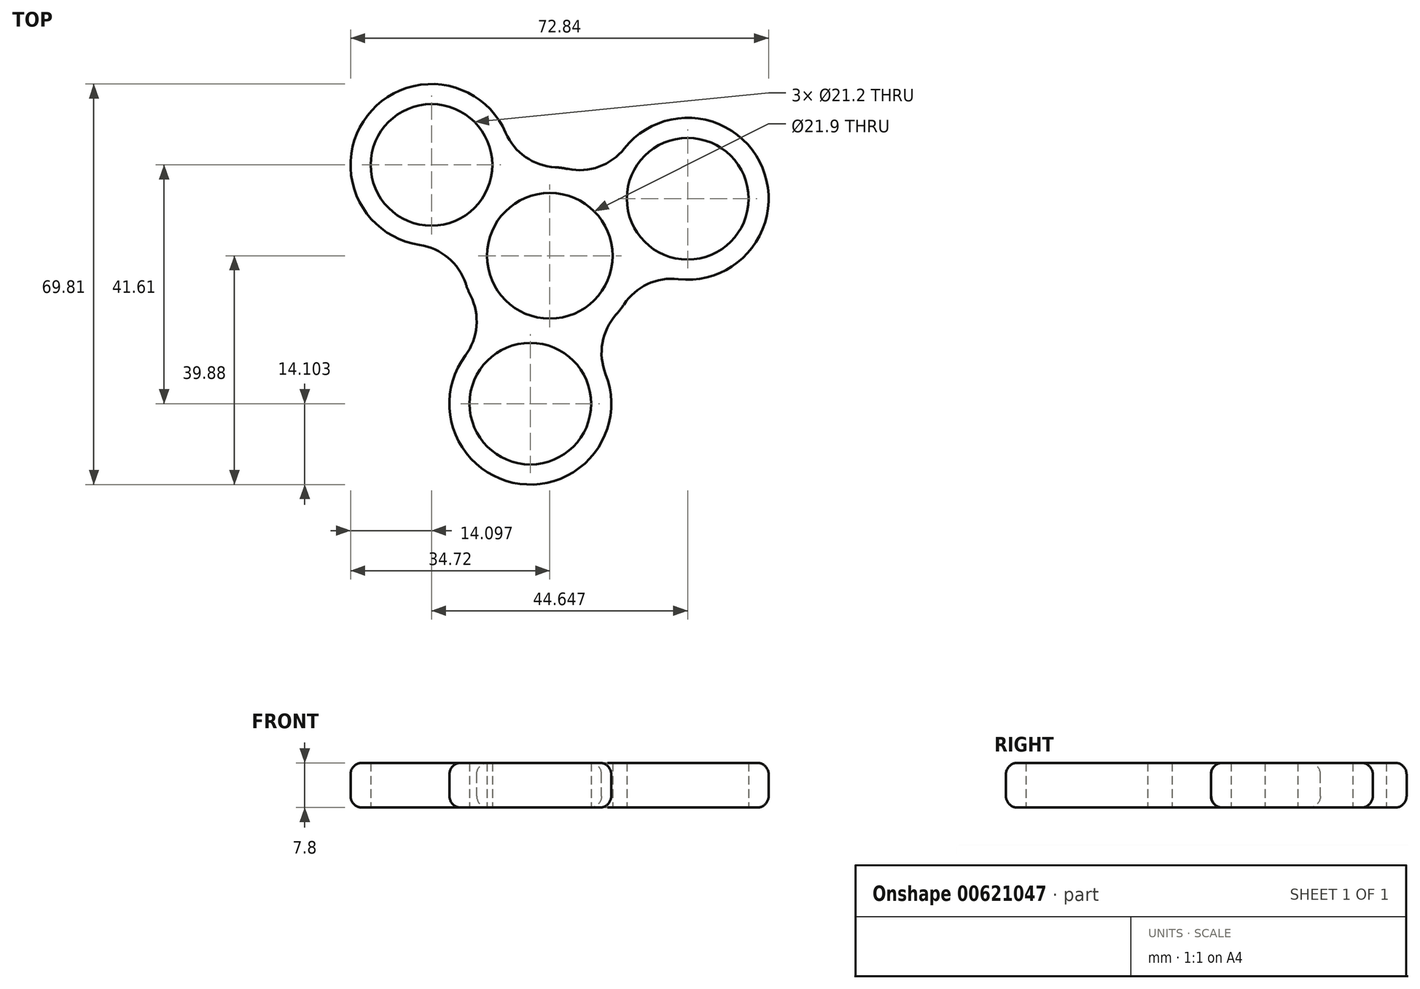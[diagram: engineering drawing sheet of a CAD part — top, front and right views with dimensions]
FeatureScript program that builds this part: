
annotation { "Feature Type Name" : "Feature", "Feature Type Description" : "" }
export const myFeature = defineFeature(function(context is Context, id is Id, definition is map)
    precondition{}
    {
        {
            var Q0;
            Q0=qCreatedBy(makeId("Top.planeOp"),FACE);
            var sketch = newSketch(context, id + "F0", { "sketchPlane" : qUnion([Q0])});
            skCircle(sketch, "E0", {"center": v(0, 0) * mm, "radius": 10.95 * mm});
            skCircle(sketch, "E1.0", {"center": v(0, 0) * mm, "radius": 15.45 * mm});
            skCircle(sketch, "E2.cCircle", {"center": v(0, 0) * mm, "radius": 13 * mm, "construction": true});
            skLineSegment(sketch, "E2.0", {"start": v(-20.62, 15.83) * mm, "end": v(24.02, 9.94) * mm, "construction": true});
            skLineSegment(sketch, "E2.1", {"start": v(24.02, 9.94) * mm, "end": v(-3.4, -25.78) * mm, "construction": true});
            skLineSegment(sketch, "E2.2", {"start": v(-3.4, -25.78) * mm, "end": v(-20.62, 15.83) * mm, "construction": true});
            skPoint(sketch, "E2.0.midPoint", {"position": v(1.7, 12.89) * mm});
            skCircle(sketch, "E3", {"center": v(-20.62, 15.83) * mm, "radius": 10.6 * mm});
            skCircle(sketch, "E4", {"center": v(24.02, 9.94) * mm, "radius": 10.6 * mm});
            skCircle(sketch, "E5", {"center": v(-3.4, -25.78) * mm, "radius": 10.6 * mm});
            skCircle(sketch, "E6.0", {"center": v(-20.62, 15.83) * mm, "radius": 14.1 * mm});
            skCircle(sketch, "E7.0", {"center": v(24.02, 9.94) * mm, "radius": 14.1 * mm});
            skCircle(sketch, "E8.0", {"center": v(-3.4, -25.78) * mm, "radius": 14.1 * mm});
            skSolve(sketch);
        }
        {
            var Q0;
            Q0=qSketchRegion(id+"F0",true);
            extrude(context, id + "F1", {"entities" : qUnion([Q0]), "depth" : 7.8 * mm, "offsetDistance" : 25 * mm});
        }
        {
            var Q0;
            {var subQ0=sQuery(id+"F0.wireOp",EDGE,"E6.0");var subQ1=sQuery(id+"F0.wireOp",EDGE,"E1.0");Q0=makeQuery(id+"F1.opExtrude","SWEPT_EDGE",EDGE,{"disambiguationData":[OSD([subQ1,subQ0]),TDD([makeQuery(id+"F0.imprint","INTERSECT",VERTEX,{"disambiguationData":[OD(1.0)],"derivedFrom":[subQ1,subQ0]})])]});}
            var Q1;
            {var subQ0=sQuery(id+"F0.wireOp",EDGE,"E6.0");var subQ1=sQuery(id+"F0.wireOp",EDGE,"E1.0");Q1=makeQuery(id+"F1.opExtrude","SWEPT_EDGE",EDGE,{"disambiguationData":[OSD([subQ1,subQ0]),TDD([makeQuery(id+"F0.imprint","INTERSECT",VERTEX,{"disambiguationData":[OD(0.0)],"derivedFrom":[subQ1,subQ0]})])]});}
            var Q2;
            {var subQ0=sQuery(id+"F0.wireOp",EDGE,"E7.0");var subQ1=sQuery(id+"F0.wireOp",EDGE,"E1.0");Q2=makeQuery(id+"F1.opExtrude","SWEPT_EDGE",EDGE,{"disambiguationData":[OSD([subQ1,subQ0]),TDD([makeQuery(id+"F0.imprint","INTERSECT",VERTEX,{"disambiguationData":[OD(0.0)],"derivedFrom":[subQ1,subQ0]})])]});}
            var Q3;
            {var subQ0=sQuery(id+"F0.wireOp",EDGE,"E7.0");var subQ1=sQuery(id+"F0.wireOp",EDGE,"E1.0");Q3=makeQuery(id+"F1.opExtrude","SWEPT_EDGE",EDGE,{"disambiguationData":[OSD([subQ1,subQ0]),TDD([makeQuery(id+"F0.imprint","INTERSECT",VERTEX,{"disambiguationData":[OD(1.0)],"derivedFrom":[subQ1,subQ0]})])]});}
            var Q4;
            {var subQ0=sQuery(id+"F0.wireOp",EDGE,"E8.0");var subQ1=sQuery(id+"F0.wireOp",EDGE,"E1.0");Q4=makeQuery(id+"F1.opExtrude","SWEPT_EDGE",EDGE,{"disambiguationData":[OSD([subQ1,subQ0]),TDD([makeQuery(id+"F0.imprint","INTERSECT",VERTEX,{"disambiguationData":[OD(1.0)],"derivedFrom":[subQ1,subQ0]})])]});}
            var Q5;
            {var subQ0=sQuery(id+"F0.wireOp",EDGE,"E8.0");var subQ1=sQuery(id+"F0.wireOp",EDGE,"E1.0");Q5=makeQuery(id+"F1.opExtrude","SWEPT_EDGE",EDGE,{"disambiguationData":[OSD([subQ1,subQ0]),TDD([makeQuery(id+"F0.imprint","INTERSECT",VERTEX,{"disambiguationData":[OD(0.0)],"derivedFrom":[subQ1,subQ0]})])]});}
            fillet(context, id + "F2", {"entities" : qUnion([Q0, Q1, Q2, Q3, Q4, Q5]), "radius" : 10 * mm, "tangentPropagation" : true, "allowEdgeOverflow" : false});
        }
        {
            var Q0;
            {var subQ0=sQuery(id+"F0.wireOp",EDGE,"E7.0");var subQ1=sQuery(id+"F0.wireOp",EDGE,"E1.0");Q0=makeQuery(id+"F2.opFillet","BLEND_EDGE",EDGE,{"blendedFrom":[makeQuery(id+"F1.opExtrude","SWEPT_EDGE",EDGE,{"disambiguationData":[OSD([subQ1,subQ0]),TDD([makeQuery(id+"F0.imprint","INTERSECT",VERTEX,{"disambiguationData":[OD(1.0)],"derivedFrom":[subQ1,subQ0]})])]}),makeQuery(id+"F1.opExtrude","CAP_FACE",FACE,{"disambiguationData":[OSD([sQuery(id+"F0.wireOp",EDGE,"E0"),subQ1,sQuery(id+"F0.wireOp",EDGE,"E3"),sQuery(id+"F0.wireOp",EDGE,"E4"),sQuery(id+"F0.wireOp",EDGE,"E5"),sQuery(id+"F0.wireOp",EDGE,"E6.0"),subQ0,sQuery(id+"F0.wireOp",EDGE,"E8.0")])],"isStart":true})],"blendedInto":[makeQuery(id+"F1.opExtrude","CAP_FACE",FACE,{"disambiguationData":[OSD([sQuery(id+"F0.wireOp",EDGE,"E0"),subQ1,sQuery(id+"F0.wireOp",EDGE,"E3"),sQuery(id+"F0.wireOp",EDGE,"E4"),sQuery(id+"F0.wireOp",EDGE,"E5"),sQuery(id+"F0.wireOp",EDGE,"E6.0"),subQ0,sQuery(id+"F0.wireOp",EDGE,"E8.0")])],"isStart":true})]});}
            var Q1;
            {var subQ0=sQuery(id+"F0.wireOp",EDGE,"E8.0");var subQ1=sQuery(id+"F0.wireOp",EDGE,"E1.0");Q1=makeQuery(id+"F2.opFillet","BLEND_EDGE",EDGE,{"blendedFrom":[makeQuery(id+"F1.opExtrude","SWEPT_EDGE",EDGE,{"disambiguationData":[OSD([subQ1,subQ0]),TDD([makeQuery(id+"F0.imprint","INTERSECT",VERTEX,{"disambiguationData":[OD(0.0)],"derivedFrom":[subQ1,subQ0]})])]}),makeQuery(id+"F1.opExtrude","CAP_FACE",FACE,{"disambiguationData":[OSD([sQuery(id+"F0.wireOp",EDGE,"E0"),subQ1,sQuery(id+"F0.wireOp",EDGE,"E3"),sQuery(id+"F0.wireOp",EDGE,"E4"),sQuery(id+"F0.wireOp",EDGE,"E5"),sQuery(id+"F0.wireOp",EDGE,"E6.0"),sQuery(id+"F0.wireOp",EDGE,"E7.0"),subQ0])],"isStart":false})],"blendedInto":[makeQuery(id+"F1.opExtrude","CAP_FACE",FACE,{"disambiguationData":[OSD([sQuery(id+"F0.wireOp",EDGE,"E0"),subQ1,sQuery(id+"F0.wireOp",EDGE,"E3"),sQuery(id+"F0.wireOp",EDGE,"E4"),sQuery(id+"F0.wireOp",EDGE,"E5"),sQuery(id+"F0.wireOp",EDGE,"E6.0"),sQuery(id+"F0.wireOp",EDGE,"E7.0"),subQ0])],"isStart":false})]});}
            fillet(context, id + "F3", {"entities" : qUnion([Q0, Q1]), "radius" : 2 * mm, "tangentPropagation" : true, "allowEdgeOverflow" : false});
        }
    });
